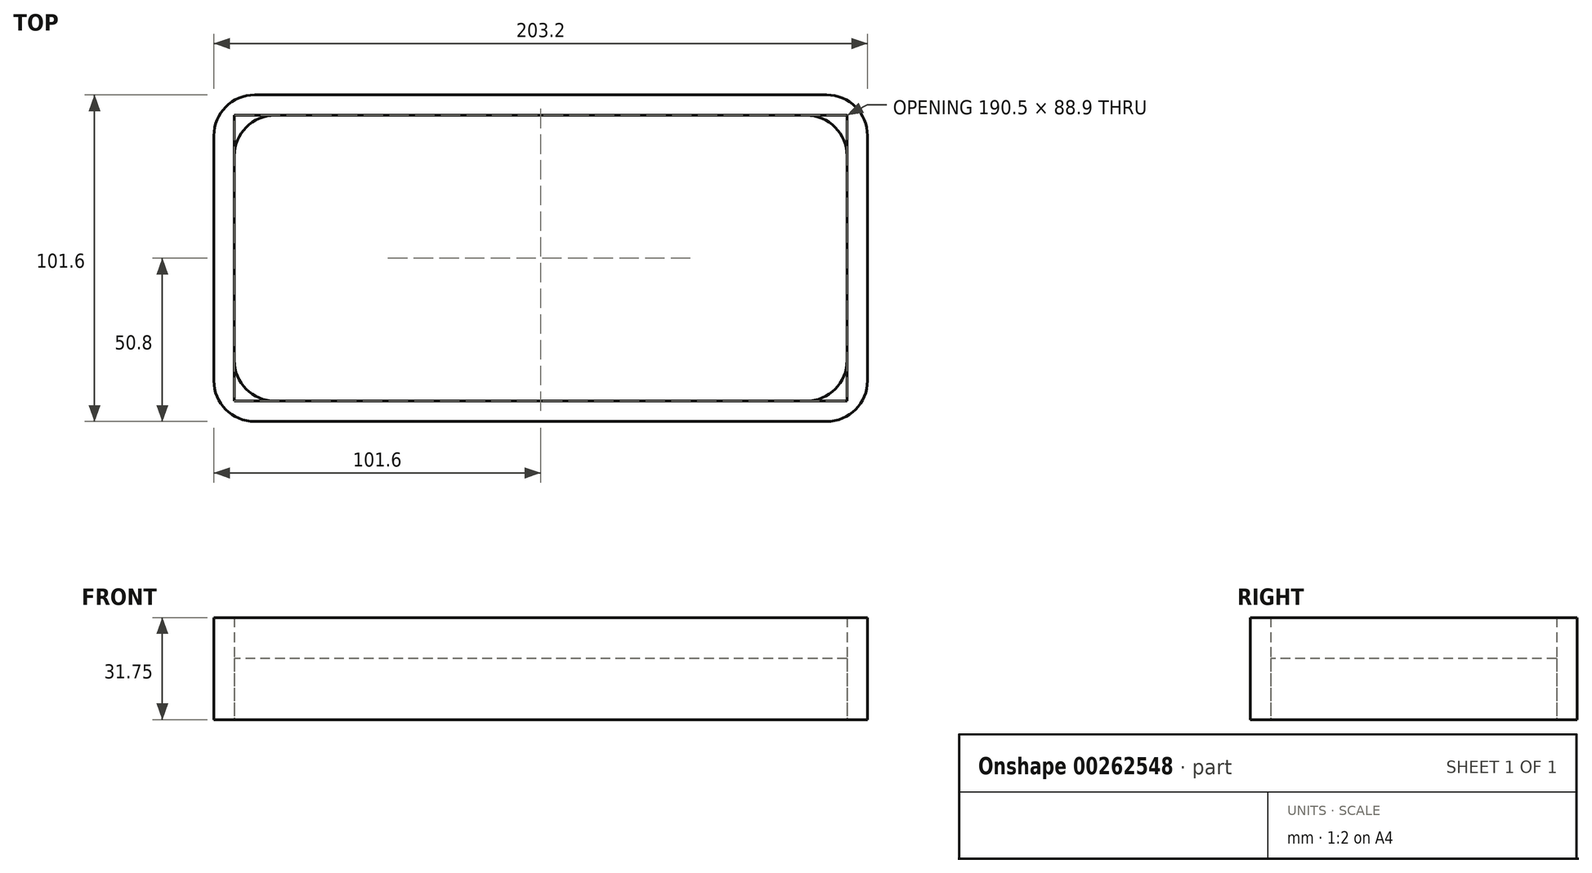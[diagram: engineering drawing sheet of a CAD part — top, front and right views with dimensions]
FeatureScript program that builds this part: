
annotation { "Feature Type Name" : "Feature", "Feature Type Description" : "" }
export const myFeature = defineFeature(function(context is Context, id is Id, definition is map)
    precondition{}
    {
        {
            var Q0;
            Q0=qCreatedBy(makeId("Top.planeOp"),FACE);
            var sketch = newSketch(context, id + "F0", { "sketchPlane" : qUnion([Q0])});
            skLineSegment(sketch, "E0.bottom", {"start": v(101.6, 50.8) * mm, "end": v(-101.6, 50.8) * mm});
            skLineSegment(sketch, "E0.top", {"start": v(101.6, -50.8) * mm, "end": v(-101.6, -50.8) * mm});
            skLineSegment(sketch, "E0.left", {"start": v(101.6, 50.8) * mm, "end": v(101.6, -50.8) * mm});
            skLineSegment(sketch, "E0.right", {"start": v(-101.6, 50.8) * mm, "end": v(-101.6, -50.8) * mm});
            skPoint(sketch, "E0.middle", {"position": v(0, 0) * mm});
            skLineSegment(sketch, "E1.bottom", {"start": v(95.25, 44.45) * mm, "end": v(-95.25, 44.45) * mm});
            skLineSegment(sketch, "E1.top", {"start": v(95.25, -44.45) * mm, "end": v(-95.25, -44.45) * mm});
            skLineSegment(sketch, "E1.left", {"start": v(95.25, 44.45) * mm, "end": v(95.25, -44.45) * mm});
            skLineSegment(sketch, "E1.right", {"start": v(-95.25, 44.45) * mm, "end": v(-95.25, -44.45) * mm});
            skPoint(sketch, "E2", {"position": v(-82.55, 31.75) * mm});
            skPoint(sketch, "E3.MirrorP", {"position": v(82.55, 31.75) * mm});
            skPoint(sketch, "E4.MirrorP", {"position": v(-82.55, -31.75) * mm});
            skPoint(sketch, "E5.MirrorP", {"position": v(82.55, -31.75) * mm});
            skSolve(sketch);
        }
        {
            var Q0;
            Q0=makeQuery(id+"F0.imprint","IMPRINT",FACE,{"disambiguationData":[TD([[makeQuery(id+"F0.imprint","IMPRINT",EDGE,{"derivedFrom":sQuery(id+"F0.wireOp",EDGE,"E1.bottom")}),1.0]])]});
            extrude(context, id + "F1", {"entities" : qUnion([Q0]), "depth" : 19.05 * mm});
        }
        {
            var Q0;
            Q0=makeQuery(id+"F0.imprint","IMPRINT",FACE,{"disambiguationData":[TD([[makeQuery(id+"F0.imprint","IMPRINT",EDGE,{"derivedFrom":sQuery(id+"F0.wireOp",EDGE,"E0.bottom")}),1.0]])]});
            extrude(context, id + "F2", {"entities" : qUnion([Q0]), "depth" : 31.75 * mm});
        }
        {
            var Q0;
            Q0=makeQuery(id+"F2.opExtrude","SWEPT_EDGE",EDGE,{"disambiguationData":[OSD([sQuery(id+"F0.wireOp",EDGE,"E0.bottom"),sQuery(id+"F0.wireOp",EDGE,"E0.right")])]});
            var Q1;
            Q1=makeQuery(id+"F2.opExtrude","SWEPT_EDGE",EDGE,{"disambiguationData":[OSD([sQuery(id+"F0.wireOp",EDGE,"E0.top"),sQuery(id+"F0.wireOp",EDGE,"E0.right")])]});
            var Q2;
            Q2=makeQuery(id+"F2.opExtrude","SWEPT_EDGE",EDGE,{"disambiguationData":[OSD([sQuery(id+"F0.wireOp",EDGE,"E0.top"),sQuery(id+"F0.wireOp",EDGE,"E0.left")])]});
            var Q3;
            Q3=makeQuery(id+"F2.opExtrude","SWEPT_EDGE",EDGE,{"disambiguationData":[OSD([sQuery(id+"F0.wireOp",EDGE,"E0.bottom"),sQuery(id+"F0.wireOp",EDGE,"E0.left")])]});
            var Q4;
            Q4=makeQuery(id+"F2.opExtrude","SWEPT_EDGE",EDGE,{"disambiguationData":[OSD([sQuery(id+"F0.wireOp",EDGE,"E1.bottom"),sQuery(id+"F0.wireOp",EDGE,"E1.right")])]});
            var Q5;
            Q5=makeQuery(id+"F2.opExtrude","SWEPT_EDGE",EDGE,{"disambiguationData":[OSD([sQuery(id+"F0.wireOp",EDGE,"E1.top"),sQuery(id+"F0.wireOp",EDGE,"E1.right")])]});
            var Q6;
            Q6=makeQuery(id+"F2.opExtrude","SWEPT_EDGE",EDGE,{"disambiguationData":[OSD([sQuery(id+"F0.wireOp",EDGE,"E1.bottom"),sQuery(id+"F0.wireOp",EDGE,"E1.left")])]});
            var Q7;
            Q7=makeQuery(id+"F2.opExtrude","SWEPT_EDGE",EDGE,{"disambiguationData":[OSD([sQuery(id+"F0.wireOp",EDGE,"E1.top"),sQuery(id+"F0.wireOp",EDGE,"E1.left")])]});
            fillet(context, id + "F3", {"entities" : qUnion([Q0, Q1, Q2, Q3, Q4, Q5, Q6, Q7]), "radius" : 12.7 * mm, "tangentPropagation" : true, "allowEdgeOverflow" : false});
        }
    });
